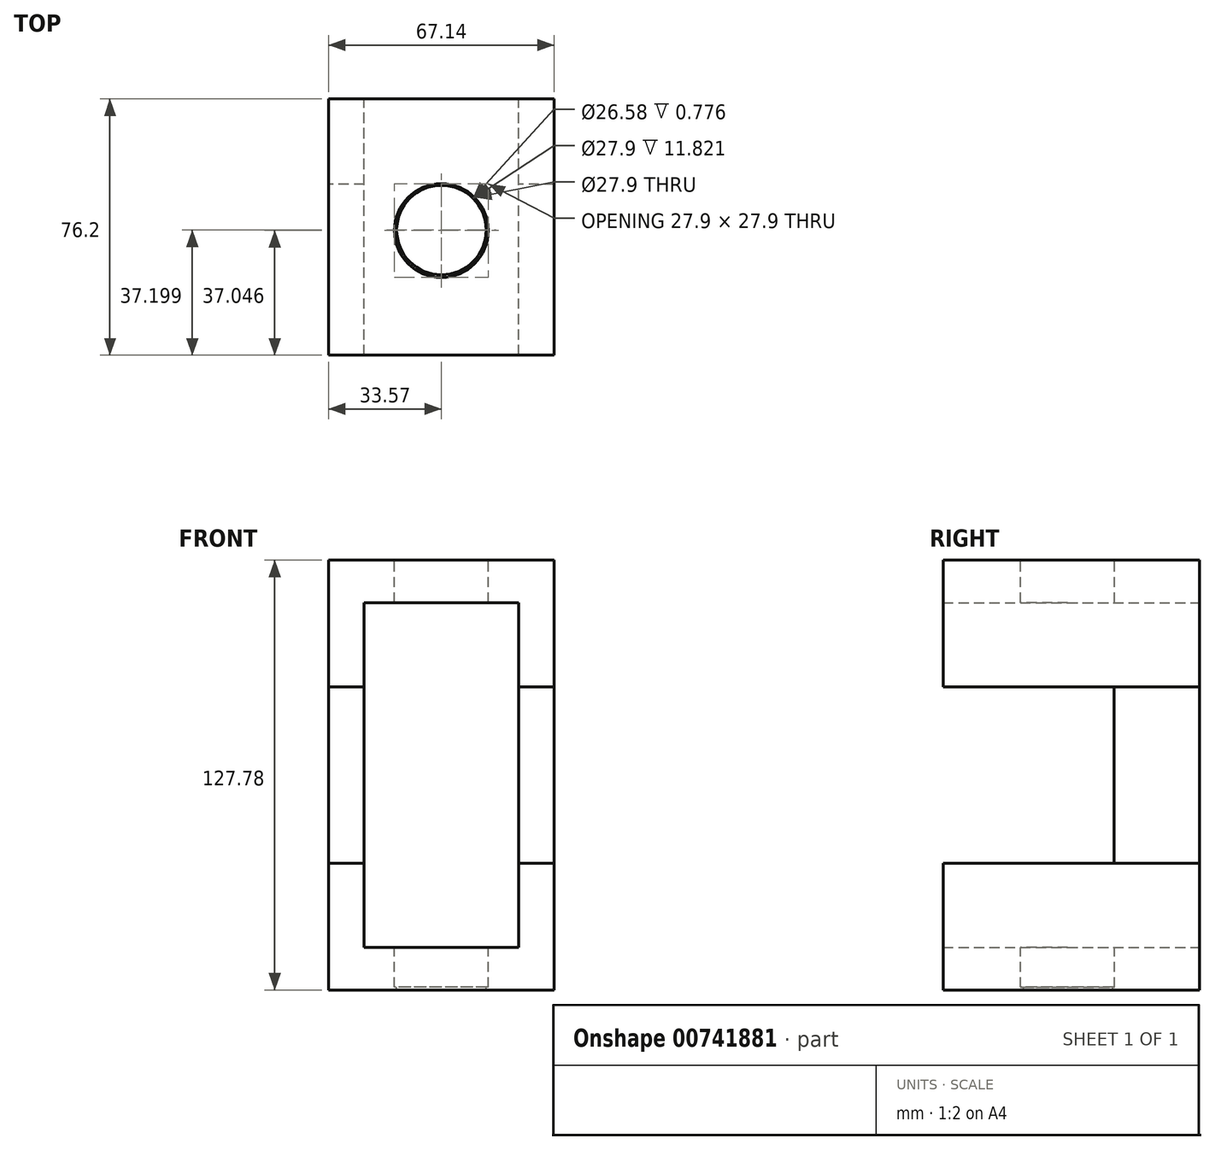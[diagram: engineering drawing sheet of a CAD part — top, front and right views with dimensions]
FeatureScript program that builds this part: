
annotation { "Feature Type Name" : "Feature", "Feature Type Description" : "" }
export const myFeature = defineFeature(function(context is Context, id is Id, definition is map)
    precondition{}
    {
        {
            var Q0;
            Q0=qCreatedBy(makeId("Front.planeOp"),FACE);
            var sketch = newSketch(context, id + "F0", { "sketchPlane" : qUnion([Q0])});
            skLineSegment(sketch, "E0.bottom", {"start": v(33.57, 63.89) * mm, "end": v(-33.57, 63.89) * mm});
            skLineSegment(sketch, "E0.top", {"start": v(33.57, -63.89) * mm, "end": v(-33.57, -63.89) * mm});
            skLineSegment(sketch, "E0.left", {"start": v(33.57, 63.89) * mm, "end": v(33.57, -63.89) * mm});
            skLineSegment(sketch, "E0.right", {"start": v(-33.57, 63.89) * mm, "end": v(-33.57, -63.89) * mm});
            skPoint(sketch, "E0.middle", {"position": v(0, 0) * mm});
            skLineSegment(sketch, "E1.bottom", {"start": v(22.98, 51.3) * mm, "end": v(-22.98, 51.3) * mm});
            skLineSegment(sketch, "E1.top", {"start": v(22.98, -51.3) * mm, "end": v(-22.98, -51.3) * mm});
            skLineSegment(sketch, "E1.left", {"start": v(22.98, 51.3) * mm, "end": v(22.98, -51.3) * mm});
            skLineSegment(sketch, "E1.right", {"start": v(-22.98, 51.3) * mm, "end": v(-22.98, -51.3) * mm});
            skLineSegment(sketch, "E2.bottom", {"start": v(56.2, 26.25) * mm, "end": v(-56.2, 26.25) * mm});
            skLineSegment(sketch, "E2.top", {"start": v(56.2, -26.25) * mm, "end": v(-56.2, -26.25) * mm});
            skLineSegment(sketch, "E2.left", {"start": v(56.2, 26.25) * mm, "end": v(56.2, -26.25) * mm});
            skLineSegment(sketch, "E2.right", {"start": v(-56.2, 26.25) * mm, "end": v(-56.2, -26.25) * mm});
            skSolve(sketch);
        }
        {
            var Q0;
            {var subQ7=sQuery(id+"F0.wireOp",EDGE,"E0.bottom");Q0=makeQuery(id+"F0.imprint","IMPRINT",FACE,{"disambiguationData":[TD([[makeQuery(id+"F0.imprint","IMPRINT",EDGE,{"derivedFrom":subQ7}),1.0]])]});}
            extrude(context, id + "F1", {"entities" : qUnion([Q0]), "depth" : 76.2 * mm, "offsetDistance" : 25.4 * mm});
        }
        {
            var Q0;
            {var subQ1=sQuery(id+"F0.wireOp",EDGE,"E0.top");Q0=makeQuery(id+"F0.imprint","IMPRINT",FACE,{"disambiguationData":[TD([[makeQuery(id+"F0.imprint","IMPRINT",EDGE,{"derivedFrom":subQ1}),-1.0]])]});}
            extrude(context, id + "F2", {"entities" : qUnion([Q0]), "depth" : 76.2 * mm, "offsetDistance" : 25.4 * mm});
        }
        {
            var Q0;
            {var subQ0=sQuery(id+"F0.wireOp",EDGE,"E2.bottom");var subQ1=sQuery(id+"F0.wireOp",EDGE,"E0.right");var subQ2=makeQuery(id+"F0.imprint","INTERSECT",VERTEX,{"derivedFrom":[subQ1,subQ0]});Q0=makeQuery(id+"F0.imprint","IMPRINT",FACE,{"disambiguationData":[TD([[makeQuery(id+"F0.imprint","IMPRINT",EDGE,{"disambiguationData":[TD([[subQ2,-1.0]])],"derivedFrom":subQ1}),1.0]])]});}
            extrude(context, id + "F3", {"entities" : qUnion([Q0]), "depth" : 25.4 * mm, "offsetDistance" : 25.4 * mm});
        }
        {
            var Q0;
            {var subQ0=sQuery(id+"F0.wireOp",EDGE,"E2.bottom");var subQ1=sQuery(id+"F0.wireOp",EDGE,"E0.left");var subQ2=makeQuery(id+"F0.imprint","INTERSECT",VERTEX,{"derivedFrom":[subQ1,subQ0]});Q0=makeQuery(id+"F0.imprint","IMPRINT",FACE,{"disambiguationData":[TD([[makeQuery(id+"F0.imprint","IMPRINT",EDGE,{"disambiguationData":[TD([[subQ2,-1.0]])],"derivedFrom":subQ1}),-1.0]])]});}
            extrude(context, id + "F4", {"entities" : qUnion([Q0]), "depth" : 25.4 * mm, "offsetDistance" : 25.4 * mm});
        }
        {
            var Q0;
            Q0=qCreatedBy(makeId("Top.planeOp"),FACE);
            var sketch = newSketch(context, id + "F5", { "sketchPlane" : qUnion([Q0])});
            skCircle(sketch, "E3", {"center": v(0, -39) * mm, "radius": 13.29 * mm});
            skSolve(sketch);
        }
        {
            var Q0;
            Q0=makeQuery(id+"F5.imprint","IMPRINT",FACE,{"disambiguationData":[TD([[makeQuery(id+"F5.imprint","IMPRINT",EDGE,{"derivedFrom":sQuery(id+"F5.wireOp",EDGE,"E3")}),1.0]])]});
            extrude(context, id + "F6", {"entities" : qUnion([Q0]), "operationType" : NewBodyOperationType.REMOVE, "oppositeDirection" : true, "depth" : 127 * mm, "offsetDistance" : 25.4 * mm, "hasSecondDirection" : true, "secondDirectionOppositeDirection" : true, "secondDirectionDepth" : 13.2 * mm});
        }
        {
            var Q0;
            Q0=makeQuery(id+"F1.opExtrude","SWEPT_FACE",FACE,{"disambiguationData":[OSD([sQuery(id+"F0.wireOp",EDGE,"E0.bottom")])]});
            var sketch = newSketch(context, id + "F7", { "sketchPlane" : qUnion([Q0])});
            skCircle(sketch, "E4", {"center": v(0, -39.15) * mm, "radius": 13.95 * mm});
            skSolve(sketch);
        }
        {
            var Q0;
            Q0 = qSketchRegion(id + "F7", true);
            extrude(context, id + "F8", {"entities" : qUnion([Q0]), "operationType" : NewBodyOperationType.REMOVE, "oppositeDirection" : true, "depth" : 127 * mm, "offsetDistance" : 25.4 * mm});
        }
    });
